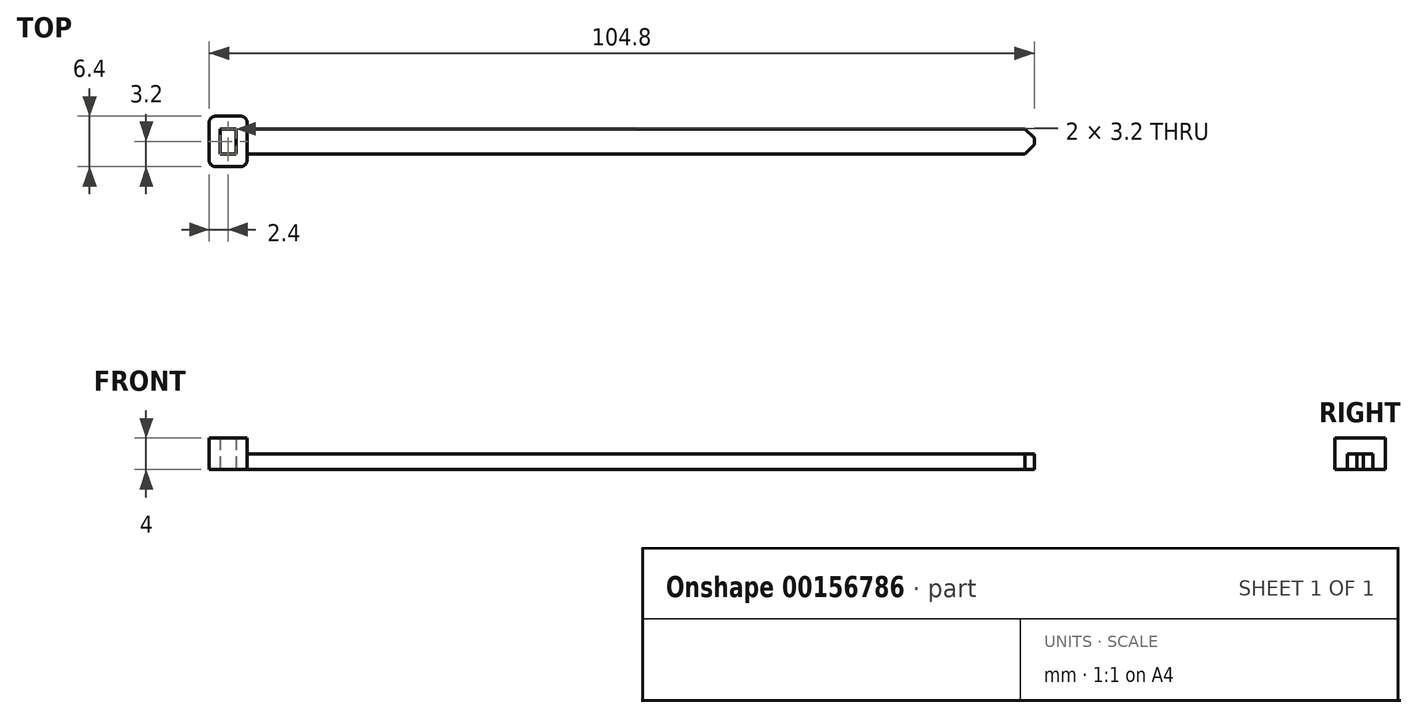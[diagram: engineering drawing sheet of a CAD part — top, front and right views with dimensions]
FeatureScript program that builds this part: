
annotation { "Feature Type Name" : "Feature", "Feature Type Description" : "" }
export const myFeature = defineFeature(function(context is Context, id is Id, definition is map)
    precondition{}
    {
        {
            var Q0;
            Q0=qCreatedBy(makeId("Top.planeOp"),FACE);
            var sketch = newSketch(context, id + "F0", { "sketchPlane" : qUnion([Q0])});
            skLineSegment(sketch, "E0.bottom", {"start": v(50, -1.6) * mm, "end": v(-50, -1.6) * mm});
            skLineSegment(sketch, "E0.top", {"start": v(50, 1.6) * mm, "end": v(-50, 1.6) * mm});
            skLineSegment(sketch, "E0.left", {"start": v(50, -1.6) * mm, "end": v(50, 1.6) * mm});
            skLineSegment(sketch, "E0.right", {"start": v(-50, -1.6) * mm, "end": v(-50, 1.6) * mm});
            skPoint(sketch, "E0.middle", {"position": v(0, 0) * mm});
            skSolve(sketch);
        }
        {
            var Q0;
            Q0 = qSketchRegion(id + "F0", true);
            extrude(context, id + "F1", {"entities" : qUnion([Q0]), "depth" : 2 * mm});
        }
        {
            var Q0;
            Q0=makeQuery(id+"F1.opExtrude","SWEPT_EDGE",EDGE,{"disambiguationData":[OSD([sQuery(id+"F0.wireOp",EDGE,"E0.top"),sQuery(id+"F0.wireOp",EDGE,"E0.left")])]});
            var Q1;
            Q1=makeQuery(id+"F1.opExtrude","SWEPT_EDGE",EDGE,{"disambiguationData":[OSD([sQuery(id+"F0.wireOp",EDGE,"E0.bottom"),sQuery(id+"F0.wireOp",EDGE,"E0.left")])]});
            chamfer(context, id + "F2", {"entities" : qUnion([Q0, Q1]), "width" : 1.2 * mm, "tangentPropagation" : true});
        }
        {
            var Q0;
            Q0=qCreatedBy(makeId("Top.planeOp"),FACE);
            var sketch = newSketch(context, id + "F3", { "sketchPlane" : qUnion([Q0])});
            skLineSegment(sketch, "E1.bottom", {"start": v(-50, -3.2) * mm, "end": v(-54.8, -3.2) * mm});
            skLineSegment(sketch, "E1.top", {"start": v(-50, 3.2) * mm, "end": v(-54.8, 3.2) * mm});
            skLineSegment(sketch, "E1.left", {"start": v(-50, -3.2) * mm, "end": v(-50, 3.2) * mm});
            skLineSegment(sketch, "E1.right", {"start": v(-54.8, -3.2) * mm, "end": v(-54.8, 3.2) * mm});
            skPoint(sketch, "E1.middle", {"position": v(-52.4, 0) * mm});
            skLineSegment(sketch, "E2.bottom", {"start": v(-51.4, -1.6) * mm, "end": v(-53.4, -1.6) * mm});
            skLineSegment(sketch, "E2.top", {"start": v(-51.4, 1.6) * mm, "end": v(-53.4, 1.6) * mm});
            skLineSegment(sketch, "E2.left", {"start": v(-51.4, -1.6) * mm, "end": v(-51.4, 1.6) * mm});
            skLineSegment(sketch, "E2.right", {"start": v(-53.4, -1.6) * mm, "end": v(-53.4, 1.6) * mm});
            skSolve(sketch);
        }
        {
            var Q0;
            Q0 = qSketchRegion(id + "F3", true);
            extrude(context, id + "F4", {"entities" : qUnion([Q0]), "operationType" : NewBodyOperationType.ADD, "depth" : 4 * mm});
        }
        {
            var Q0;
            Q0=makeQuery(id+"F4.opExtrude","SWEPT_EDGE",EDGE,{"disambiguationData":[OSD([sQuery(id+"F3.wireOp",EDGE,"E1.top"),sQuery(id+"F3.wireOp",EDGE,"E1.right")])]});
            var Q1;
            Q1=makeQuery(id+"F4.opExtrude","SWEPT_EDGE",EDGE,{"disambiguationData":[OSD([sQuery(id+"F3.wireOp",EDGE,"E1.top"),sQuery(id+"F3.wireOp",EDGE,"E1.left")])]});
            var Q2;
            Q2=makeQuery(id+"F4.opExtrude","SWEPT_EDGE",EDGE,{"disambiguationData":[OSD([sQuery(id+"F3.wireOp",EDGE,"E1.bottom"),sQuery(id+"F3.wireOp",EDGE,"E1.left")])]});
            var Q3;
            Q3=makeQuery(id+"F4.opExtrude","SWEPT_EDGE",EDGE,{"disambiguationData":[OSD([sQuery(id+"F3.wireOp",EDGE,"E1.bottom"),sQuery(id+"F3.wireOp",EDGE,"E1.right")])]});
            fillet(context, id + "F5", {"entities" : qUnion([Q0, Q1, Q2, Q3]), "radius" : .8 * mm, "tangentPropagation" : true, "allowEdgeOverflow" : false});
        }
    });
